# Revit family: 6a4d90ffea3148d08faefaeea9900682
name_source: partatom
category: Windows
units: mm (PartAtom-declared; Revit-internal decimal feet)

## family parameters
Always vertical = Yes
Cut with Voids When Loaded = No
Host = Wall
OmniClass Number = 23.30.20.00
OmniClass Title = Windows
Room Calculation Point = No
Seek Item ID = Window-Square Opening-0000-CAN-ENU
Shared = No

## types (9) — shared parameters
zero-valued in all types: Height, Width

## per-type parameters (varying)
| type | Rough Height | Rough Width | Sill Height |
| 0900 x 1200mm | 1200 mm | 900 mm  [stored 2.95276 ft] | 900 mm  [stored 2.95276 ft] |
| 0900 x 600mm | 600 mm | 900 mm  [stored 2.95276 ft] | 900 mm  [stored 2.95276 ft] |
| 0900 x 1800mm | 1800 mm  [stored 5.90551 ft] | 900 mm  [stored 2.95276 ft] | 600 mm |
| 0600 x 1800mm | 1800 mm  [stored 5.90551 ft] | 600 mm | 600 mm |
| 0600 x 1200mm | 1200 mm | 600 mm | 900 mm  [stored 2.95276 ft] |
| 0600 x 600mm | 600 mm | 600 mm | 900 mm  [stored 2.95276 ft] |
| 0400 x 600mm | 600 mm | 400 mm  [stored 1.31234 ft] | 900 mm  [stored 2.95276 ft] |
| 0400 x 1200mm | 1200 mm | 400 mm  [stored 1.31234 ft] | 900 mm  [stored 2.95276 ft] |
| 0400 x 1800mm | 1800 mm  [stored 5.90551 ft] | 400 mm  [stored 1.31234 ft] | 600 mm |

note: [stored X ft] marks values corroborated as IEEE doubles in the binary element streams (Revit-internal decimal feet)

## geometry (parser evidence)
native form markers: Sweep x2
no freeform markers — native parametric forms only
